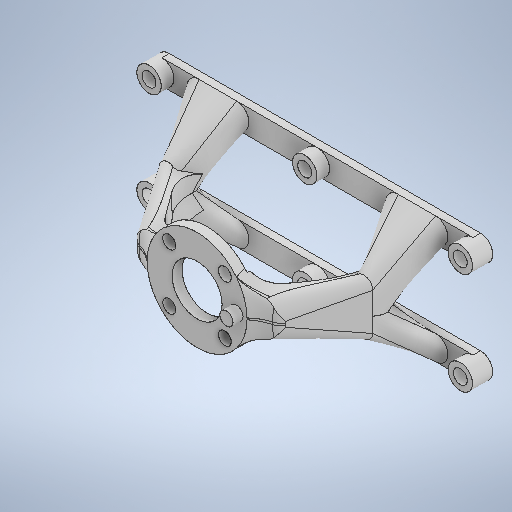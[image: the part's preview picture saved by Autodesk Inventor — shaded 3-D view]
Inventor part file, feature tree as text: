
AUTODESK INVENTOR PART (.ipt)
format: ipt  version: 2025.1 (Build 291241000, 241)  size: 1,220,608 bytes
history: native  units: mm
features: sketch x7, loft x6, extrude x5, fillet x5, plane x2
ambient origin geometry x8: Origin, YZ Plane, XZ Plane, XY Plane, X Axis, Y Axis, Z Axis, Center Point
bodies: Solid1 (feature_tree)
feature tree (25):
  sketch  "Sketch1"  dims[d0=20.0mm d1=40.0mm]
  extrude  "Extrusion1"  Depth=40.0mm
  extrude  "Extrusion2"  Depth=5.2mm
  plane  "Work Plane1"
  sketch  "Sketch2"  dims[d9=5.3mm d10=4.0mm d11=0.0mm]
  plane  "Work Plane2"
  sketch  "Sketch3"  dims[d12=8.0mm d13=0.0mm d14=47.2mm]
  extrude  "Extrusion3"  Depth=40.0mm TaperAngle=360.0deg
  sketch  "Sketch4"  dims[d15=9.8mm d17=5.6mm]
  loft  "Loft1"
  loft  "Loft2"
  loft  "Loft3"
  loft  "Loft4"
  loft  "Loft5"
  loft  "Loft6"
  fillet  "Fillet1"  Radius=15.0mm
  fillet  "Fillet2"  Radius=3.0mm
  fillet  "Fillet3"  Radius=15.0mm
  fillet  "Fillet4"  Radius=15.0mm
  fillet  "Fillet5"  [1 undecoded]
  extrude  "Extrusion4"  TaperAngle=0.0deg  [1 undecoded]
  extrude  "Extrusion5"  TaperAngle=0.0deg  [1 undecoded]
  sketch  "Sketch Circular Pattern1"  dims[d2=31.5mm d3=5.2mm]
  sketch  "Sketch Rectangular Pattern1"  dims[d4=45.0deg d5=40.0mm d7=360.0deg]
  sketch  "Sketch5"  dims[d18=134.5mm d19=30.0mm d21=62.35mm d22=10.0mm d24=10.0mm d26=40.8mm d27=7.0mm d28=15.0mm d29=3.0mm d30=0.0mm d31=15.0mm d32=15.0mm d33=0.0mm d34=90.0deg d35=0.0mm d36=90.0deg d37=0.0mm d38=90.0deg d39=0.0mm d40=90.0deg d41=0.0mm d42=90.0deg d43=0.0mm d44=90.0deg d45=0.0mm d46=90.0deg d47=0.0mm d48=90.0deg d49=10.0mm d50=15.0mm d51=7.0mm d52=0.0mm d53=90.0deg d54=0.0mm d55=90.0deg d56=15.0mm d57=10.0mm d58=7.0mm d59=0.0mm d60=90.0deg d61=0.0mm d62=90.0deg d63=17.0mm d64=17.0mm d65=17.0mm d66=17.0mm d67=5.0mm d68=8.1mm d69=0.0mm d70=10.0mm d71=10.0mm d72=10.0mm d73=10.0mm d74=2.0mm d75=0.0mm]
note: 3 required parameter values undecoded (feature->parameter linkage not recoverable at this tier; creation-order binding heuristic only, values carry confidence <= 0.55)
